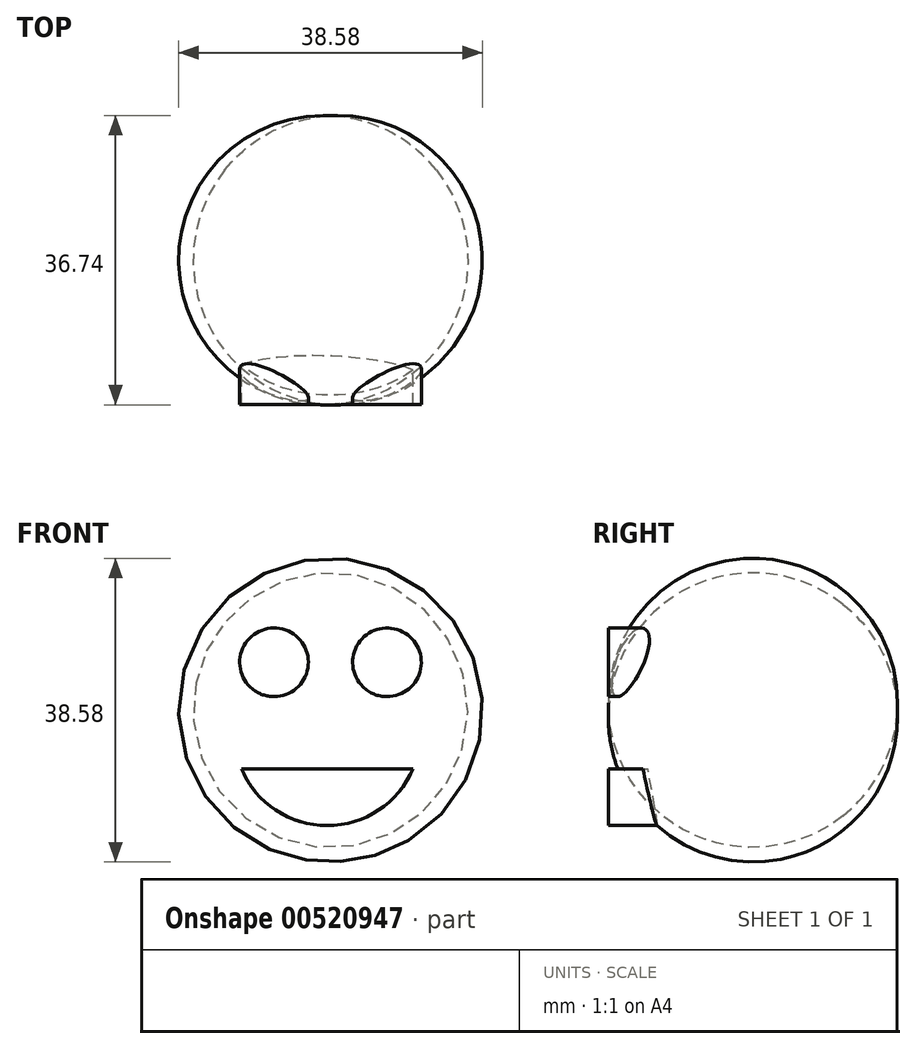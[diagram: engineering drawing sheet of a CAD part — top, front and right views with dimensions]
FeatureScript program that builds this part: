
annotation { "Feature Type Name" : "Feature", "Feature Type Description" : "" }
export const myFeature = defineFeature(function(context is Context, id is Id, definition is map)
    precondition{}
    {
        {
            var Q0;
            Q0=qCreatedBy(makeId("Top.planeOp"),FACE);
            var sketch = newSketch(context, id + "F0", { "sketchPlane" : qUnion([Q0])});
            skLineSegment(sketch, "E0", {"start": v(0, 0) * mm, "end": v(0, 36.7) * mm});
            skArc(sketch, "E1", {"start": v(0, 0) * mm, "mid": v(19.3, 18.35) * mm, "end": v(0, 36.7) * mm});
            skSolve(sketch);
        }
        {
            var Q0;
            Q0=makeQuery(id+"F0.imprint","IMPRINT",FACE,{"disambiguationData":[TD([[makeQuery(id+"F0.imprint","IMPRINT",EDGE,{"derivedFrom":sQuery(id+"F0.wireOp",EDGE,"E0")}),-1.0]])]});
            var Q1;
            Q1=sQuery(id+"F0.wireOp",EDGE,"E0");
            revolve(context, id + "F1", {"entities" : qUnion([Q0]), "axis" : qUnion([Q1]), "revolveType" : RevolveType.FULL});
        }
        {
            var Q0;
            Q0=qCreatedBy(makeId("Front.planeOp"),FACE);
            cPlane(context, id + "F2", {"entities" : qUnion([Q0]), "cplaneType" : CPlaneType.OFFSET, "offset" : 12.7 * mm, "oppositeDirection" : true, "width" : 152.4 * mm, "height" : 152.4 * mm});
        }
        {
            var Q0;
            Q0=qCreatedBy(id+"F2.planeOp",FACE);
            var sketch = newSketch(context, id + "F3", { "sketchPlane" : qUnion([Q0])});
            skCircle(sketch, "E2", {"center": v(-7.17, 6.07) * mm, "radius": 4.36 * mm});
            skCircle(sketch, "E3", {"center": v(7.17, 6.07) * mm, "radius": 4.36 * mm});
            skLineSegment(sketch, "E4", {"start": v(-11.31, -7.45) * mm, "end": v(10.48, -7.45) * mm});
            skArc(sketch, "E5", {"start": v(-11.31, -7.45) * mm, "mid": v(-0.41, -14.68) * mm, "end": v(10.48, -7.45) * mm});
            skSolve(sketch);
        }
        {
            var Q0;
            Q0 = qSketchRegion(id + "F3", true);
            extrude(context, id + "F4", {"entities" : qUnion([Q0]), "operationType" : NewBodyOperationType.ADD, "depth" : 12.7 * mm, "offsetDistance" : 25.4 * mm});
        }
    });
